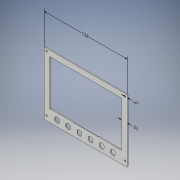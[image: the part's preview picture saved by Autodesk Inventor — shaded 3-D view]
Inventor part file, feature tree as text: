
AUTODESK INVENTOR PART (.ipt)
format: ipt  version: 2019 (Build 230136000, 136)  size: 229,888 bytes
history: native  units: in
note: dims shown in document units (in); Inventor stores cm internally (conversion verified against a paired STEP export)
features: other x4, direct_edit x3, move_body x3, extrude x2, sketch x2, imported_body x1
ambient origin geometry x8: Origin, YZ Plane, XZ Plane, XY Plane, X Axis, Y Axis, Z Axis, Center Point
bodies: Solid1 (feature_tree)
feature tree (15):
  other  "Annotations"
  direct_edit  "Direct Edit1"
  direct_edit  "Direct Edit2"
  extrude  "Extrusion1"  TaperAngle=0.0deg  [1 undecoded]
  extrude  "Extrusion2"  Depth=7.5772in
  direct_edit  "Direct Edit3"
  sketch  "Sketch1"  dims[d0=0.0in d1=0.0in d2=0.5906in d3=0.0in d4=-0.3937in d5=0.0in]
  sketch  "Sketch3"  dims[d6=0.4291in d7=0.2382in d8=0.2382in d9=2.3622in d11=1.0171in d12=0.3937in d14=0.3937in d16=0.5085in d17=0.5085in d18=6.1024in d19=0.3937in d20=0.0in d21=0.9843in d22=0.3937in d23=0.0in d27=0.0in d28=0.0in d29=0.53in d24=0.1329in d25=0.1168in d26=0.5315in d30=0.0129in d31=-0.0401in d32=0.2165in d36=0.0969in d37=0.3125in d38=7.5772in]
  imported_body  "Base1"
  move_body  "Move1"
  move_body  "Move2"
  move_body  "Move3"
  other  "Linear Dimension 1"
  other  "Linear Dimension 2"
  other  "Linear Dimension 3"
note: 1 required parameter value undecoded (feature->parameter linkage not recoverable at this tier; creation-order binding heuristic only, values carry confidence <= 0.55)
